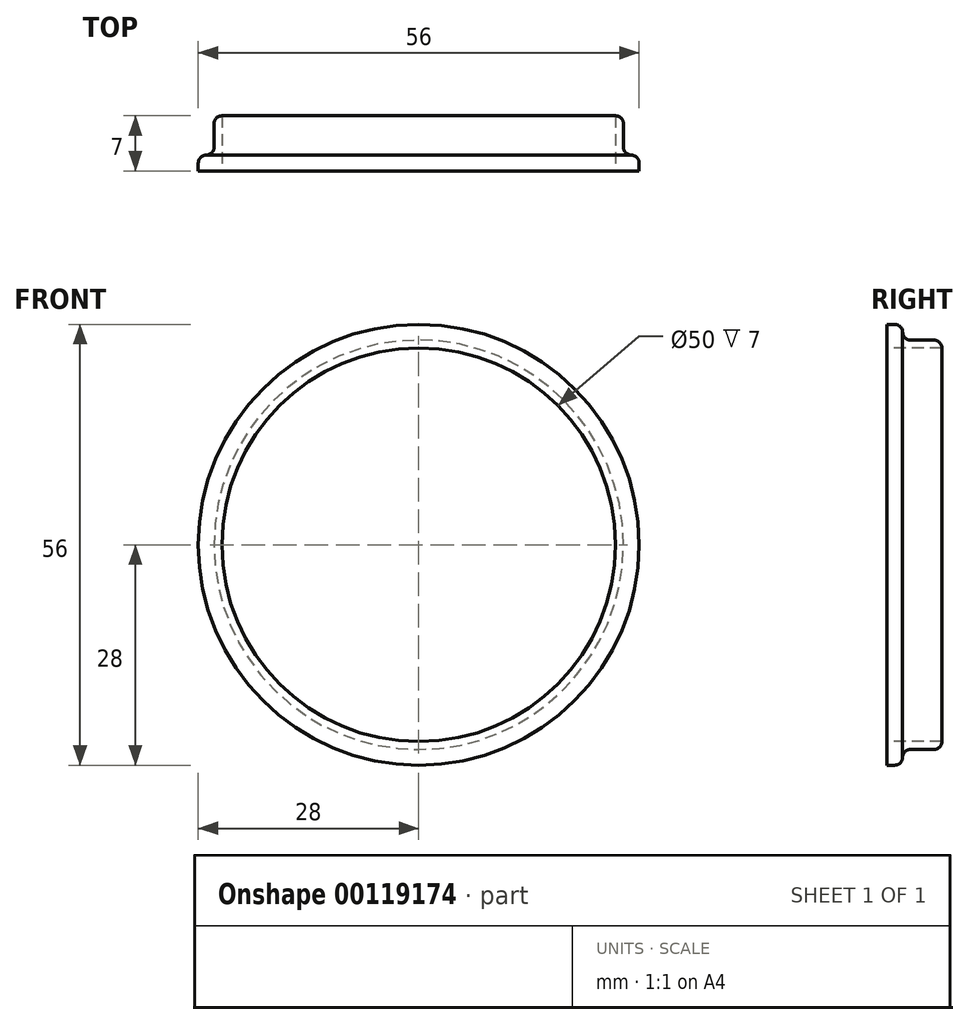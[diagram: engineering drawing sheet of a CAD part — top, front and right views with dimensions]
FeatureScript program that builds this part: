
annotation { "Feature Type Name" : "Feature", "Feature Type Description" : "" }
export const myFeature = defineFeature(function(context is Context, id is Id, definition is map)
    precondition{}
    {
        {
            var Q0;
            Q0=qCreatedBy(makeId("Top.planeOp"),FACE);
            var sketch = newSketch(context, id + "F0", { "sketchPlane" : qUnion([Q0])});
            skLineSegment(sketch, "E0", {"start": v(0, 0) * mm, "end": v(0, 13.8) * mm, "construction": true});
            skLineSegment(sketch, "E1", {"start": v(25, 0) * mm, "end": v(25, 7) * mm});
            skLineSegment(sketch, "E2", {"start": v(25, 7) * mm, "end": v(26, 7) * mm});
            skLineSegment(sketch, "E3", {"start": v(26, 7) * mm, "end": v(26, 2) * mm});
            skLineSegment(sketch, "E4", {"start": v(26, 2) * mm, "end": v(28, 2) * mm});
            skLineSegment(sketch, "E5", {"start": v(28, 2) * mm, "end": v(28, 0) * mm});
            skLineSegment(sketch, "E6", {"start": v(28, 0) * mm, "end": v(25, 0) * mm});
            skSolve(sketch);
        }
        {
            var Q0;
            Q0 = qSketchRegion(id + "F0", true);
            var Q1;
            Q1=sQuery(id+"F0.wireOp",EDGE,"E0");
            revolve(context, id + "F1", {"entities" : qUnion([Q0]), "axis" : qUnion([Q1]), "revolveType" : RevolveType.FULL});
        }
        {
            var Q0;
            Q0=makeQuery(id+"F1.opRevolve","SWEPT_EDGE",EDGE,{"disambiguationData":[OSD([sQuery(id+"F0.wireOp",EDGE,"E3"),sQuery(id+"F0.wireOp",EDGE,"E4")])]});
            var Q1;
            Q1=makeQuery(id+"F1.opRevolve","SWEPT_EDGE",EDGE,{"disambiguationData":[OSD([sQuery(id+"F0.wireOp",EDGE,"E4"),sQuery(id+"F0.wireOp",EDGE,"E5")])]});
            fillet(context, id + "F2", {"entities" : qUnion([Q0, Q1]), "radius" : 1 * mm, "tangentPropagation" : true, "allowEdgeOverflow" : false});
        }
        {
            var Q0;
            Q0=makeQuery(id+"F1.opRevolve","SWEPT_EDGE",EDGE,{"disambiguationData":[OSD([sQuery(id+"F0.wireOp",EDGE,"E2"),sQuery(id+"F0.wireOp",EDGE,"E3")])]});
            fillet(context, id + "F3", {"entities" : qUnion([Q0]), "radius" : 1 * mm, "tangentPropagation" : true, "allowEdgeOverflow" : false});
        }
    });
